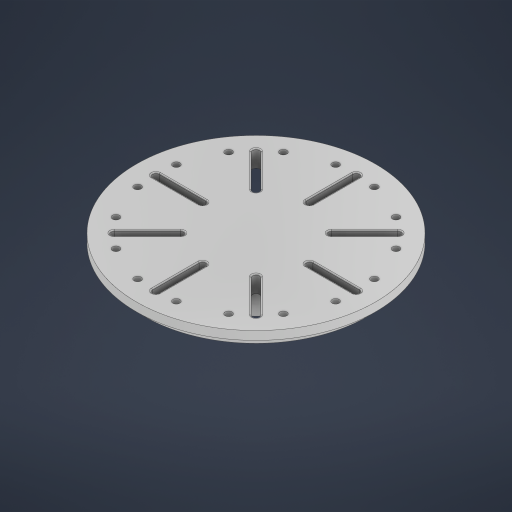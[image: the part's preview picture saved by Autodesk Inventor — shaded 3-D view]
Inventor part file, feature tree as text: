
AUTODESK INVENTOR PART (.ipt)
format: ipt  version: 2024 (Build 280153000, 153)  size: 296,448 bytes
history: native  units: mm
features: extrude x3, sketch x3, pattern_circular x1, chamfer x1, fillet x1
ambient origin geometry x8: Origin, YZ Plane, XZ Plane, XY Plane, X Axis, Y Axis, Z Axis, Center Point
bodies: Solid1 (feature_tree)
feature tree (9):
  extrude  "Extrusion1"  Depth=40.0mm TaperAngle=0.0deg
  extrude  "Extrusion2"  Depth=30.0mm TaperAngle=0.0deg
  extrude  "Extrusion3"  Depth=80.0mm TaperAngle=360.0deg
  pattern_circular  "Circular Pattern1"  Angle=45.0deg  [1 undecoded]
  chamfer  "Chamfer1"  Distance=2.0mm
  fillet  "Fillet1"  [1 undecoded]
  sketch  "Sketch1"  dims[d0=160.0mm d1=40.0mm d2=0.0mm]
  sketch  "Sketch2"  dims[d3=420.0mm d4=30.0mm d5=0.0mm]
  sketch  "Sketch3"  dims[d6=30.0mm d7=0.0mm d8=80.0mm d9=360.0deg d11=15.0mm d12=2.0mm d13=45.0deg d14=2.0mm]
note: 2 required parameter values undecoded (feature->parameter linkage not recoverable at this tier; creation-order binding heuristic only, values carry confidence <= 0.55)
